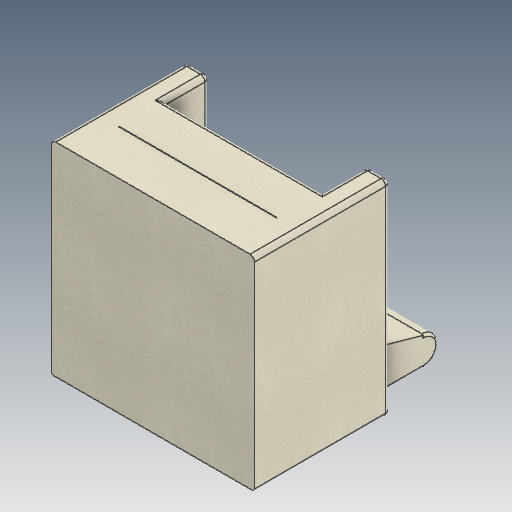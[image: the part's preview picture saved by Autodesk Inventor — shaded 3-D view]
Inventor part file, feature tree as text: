
AUTODESK INVENTOR PART (.ipt)
format: ipt  version: 2020.2 (Build 242310000, 310)  size: 324,096 bytes
history: native  units: mm
features: fillet x6, extrude x5, sketch x5, plane x3
ambient origin geometry x8: Origin, YZ Plane, XZ Plane, XY Plane, X Axis, Y Axis, Z Axis, Center Point
bodies: Solid1 (feature_tree)
feature tree (19):
  extrude  "Extrusion1"  Depth=900.0mm
  plane  "Work Plane1"
  sketch  "Sketch4"  dims[d4=0.0mm d5=2.0mm]
  fillet  "Fillet1"  Radius=200.0mm
  extrude  "Extrusion2"  Depth=2.0mm
  plane  "Work Plane2"
  extrude  "Extrusion3"  TaperAngle=0.0deg  [1 undecoded]
  fillet  "Fillet2"  Radius=600.0mm
  fillet  "Fillet3"  Radius=100.0mm
  plane  "Work Plane3"
  extrude  "Extrusion4"  Depth=20.0mm
  sketch  "Sketch7"  dims[d16=900.0mm d17=100.0mm d18=0.0mm d21=450.0mm d23=20.0mm d24=10.0mm d25=700.0mm d26=0.0mm d27=10.0mm d28=10.0mm]
  fillet  "Fillet6"  [1 undecoded]
  fillet  "Fillet7"  Radius=600.0mm
  extrude  "Extrusion5"  Depth=100.0mm TaperAngle=0.0deg
  fillet  "Fillet8"  Radius=450.0mm
  sketch  "Sketch3"  dims[d0=700.0mm d1=900.0mm d2=200.0mm d3=0.0mm]
  sketch  "Sketch5"  dims[d6=200.0mm d7=0.0mm d8=0.0mm d9=600.0mm d10=100.0mm d11=0.0mm]
  sketch  "Sketch6"  dims[d12=20.0mm d13=20.0mm d14=0.0mm d15=600.0mm]
note: 2 required parameter values undecoded (feature->parameter linkage not recoverable at this tier; creation-order binding heuristic only, values carry confidence <= 0.55)
